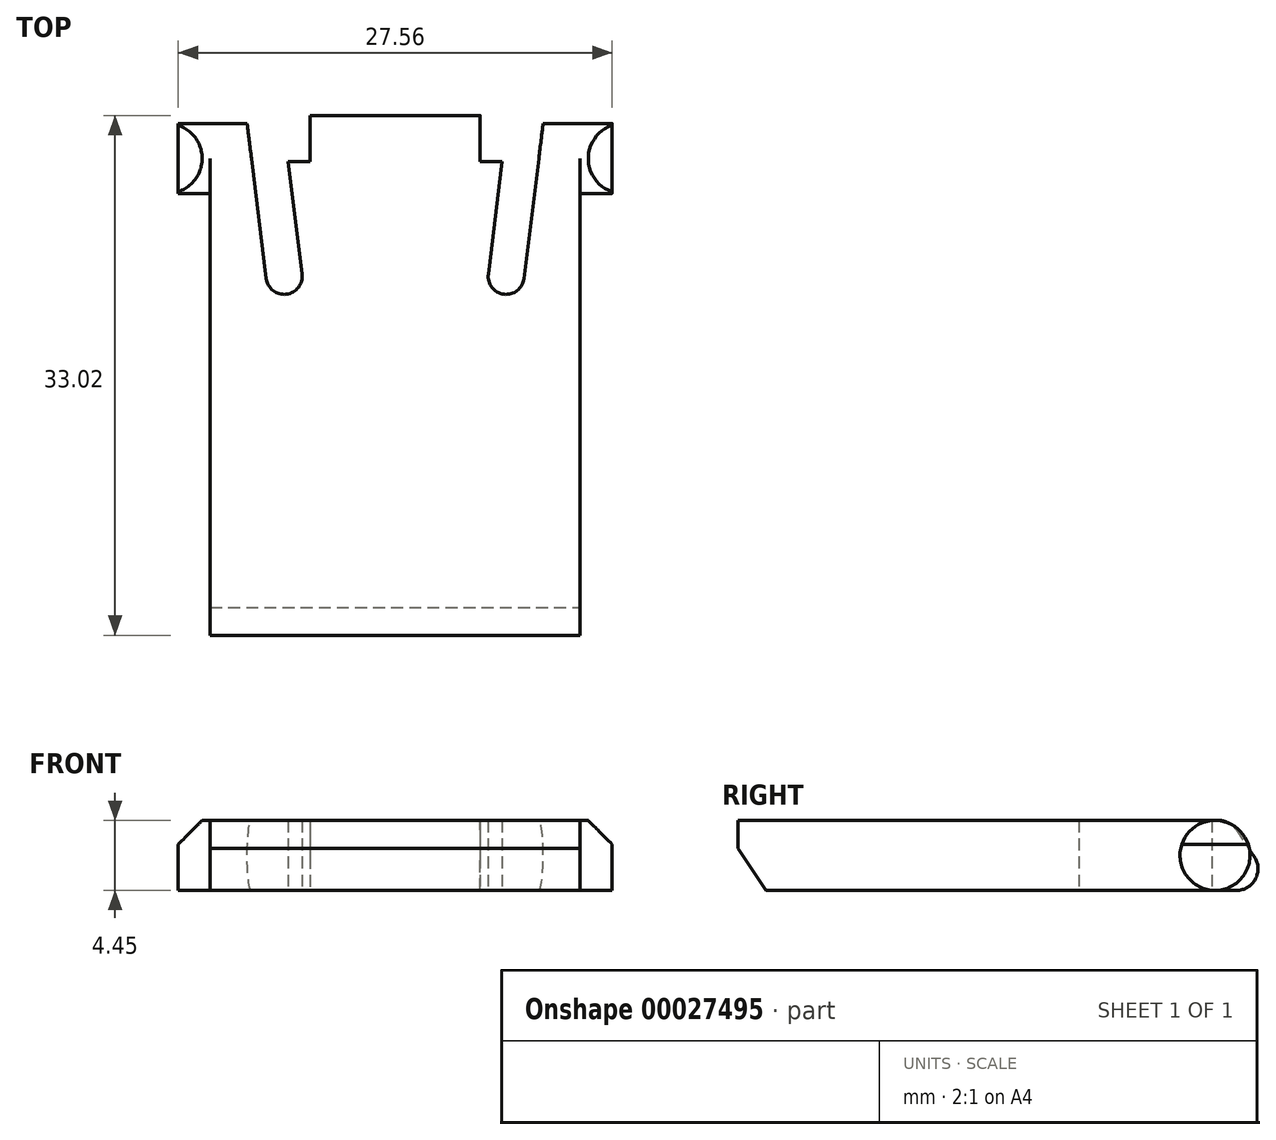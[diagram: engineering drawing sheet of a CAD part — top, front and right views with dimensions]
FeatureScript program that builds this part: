
annotation { "Feature Type Name" : "Feature", "Feature Type Description" : "" }
export const myFeature = defineFeature(function(context is Context, id is Id, definition is map)
    precondition{}
    {
        {
            var Q0;
            Q0=qCreatedBy(makeId("Top.planeOp"),FACE);
            var sketch = newSketch(context, id + "F0", { "sketchPlane" : qUnion([Q0])});
            skLineSegment(sketch, "E0.bottom", {"start": v(0, 33.02) * mm, "end": v(2.29, 33.02) * mm, "construction": true});
            skLineSegment(sketch, "E0.top", {"start": v(0, 0) * mm, "end": v(23.5, 0) * mm});
            skLineSegment(sketch, "E0.left", {"start": v(0, 33.02) * mm, "end": v(0, 32.51) * mm, "construction": true});
            skLineSegment(sketch, "E0.right", {"start": v(23.5, 33.02) * mm, "end": v(23.5, 0) * mm});
            skArc(sketch, "E1", {"start": v(3.56, 22.86) * mm, "mid": v(4.74, 21.66) * mm, "end": v(5.83, 22.94) * mm});
            skLineSegment(sketch, "E2", {"start": v(0, 22.86) * mm, "end": v(3.56, 22.86) * mm, "construction": true});
            skLineSegment(sketch, "E3", {"start": v(0.5, 33.02) * mm, "end": v(0.5, 22.86) * mm, "construction": true});
            skLineSegment(sketch, "E4", {"start": v(5.83, 22.94) * mm, "end": v(4.95, 30.1) * mm});
            skLineSegment(sketch, "E5", {"start": v(2.29, 33.02) * mm, "end": v(2.35, 32.51) * mm, "construction": true});
            skLineSegment(sketch, "E6.trimOffspring", {"start": v(6.35, 33.02) * mm, "end": v(17.15, 33.02) * mm});
            skLineSegment(sketch, "E7", {"start": v(11.75, 0) * mm, "end": v(11.75, 33.02) * mm, "construction": true});
            skLineSegment(sketch, "E8", {"start": v(4.95, 30.1) * mm, "end": v(6.35, 30.1) * mm});
            skLineSegment(sketch, "E9", {"start": v(6.35, 30.1) * mm, "end": v(6.35, 33.02) * mm});
            skLineSegment(sketch, "E10", {"start": v(0, 32.51) * mm, "end": v(2.35, 32.51) * mm});
            skLineSegment(sketch, "E11", {"start": v(2.35, 32.51) * mm, "end": v(3.56, 22.66) * mm});
            skLineSegment(sketch, "E12", {"start": v(0, 32.51) * mm, "end": v(0, 0) * mm});
            skLineSegment(sketch, "E13.MirrorCS", {"start": v(21.2, 33.02) * mm, "end": v(21.15, 32.51) * mm, "construction": true});
            skLineSegment(sketch, "E14.MirrorCS", {"start": v(23.5, 33.02) * mm, "end": v(21.2, 33.02) * mm, "construction": true});
            skLineSegment(sketch, "E15.MirrorCS", {"start": v(23.5, 33.02) * mm, "end": v(23.5, 32.51) * mm, "construction": true});
            skLineSegment(sketch, "E16.MirrorCS", {"start": v(23.5, 32.51) * mm, "end": v(21.15, 32.51) * mm});
            skLineSegment(sketch, "E17.MirrorCS", {"start": v(18.55, 30.1) * mm, "end": v(17.15, 30.1) * mm});
            skArc(sketch, "E18.MirrorCS", {"start": v(19.94, 22.86) * mm, "mid": v(18.76, 21.66) * mm, "end": v(17.66, 22.94) * mm});
            skLineSegment(sketch, "E19.MirrorCS", {"start": v(17.15, 30.1) * mm, "end": v(17.15, 33.02) * mm});
            skLineSegment(sketch, "E20.MirrorCS", {"start": v(21.15, 32.51) * mm, "end": v(19.93, 22.66) * mm});
            skLineSegment(sketch, "E21.MirrorCS", {"start": v(23, 33.02) * mm, "end": v(23, 22.86) * mm, "construction": true});
            skLineSegment(sketch, "E22.MirrorCS", {"start": v(23.5, 22.86) * mm, "end": v(19.94, 22.86) * mm, "construction": true});
            skLineSegment(sketch, "E23.MirrorCS", {"start": v(17.66, 22.94) * mm, "end": v(18.55, 30.1) * mm});
            skLineSegment(sketch, "E24.trimOffspring", {"start": v(21.2, 33.02) * mm, "end": v(23.5, 33.02) * mm, "construction": true});
            skSolve(sketch);
        }
        {
            var Q0;
            {var subQ8=sQuery(id+"F0.wireOp",EDGE,"E0.top");Q0=makeQuery(id+"F0.imprint","IMPRINT",FACE,{"disambiguationData":[TD([[makeQuery(id+"F0.imprint","IMPRINT",EDGE,{"derivedFrom":subQ8}),1.0]])]});}
            extrude(context, id + "F1", {"entities" : qUnion([Q0]), "depth" : 4.44 * mm});
        }
        {
            var Q0;
            Q0=makeQuery(id+"F1.opExtrude","SWEPT_FACE",FACE,{"disambiguationData":[OSD([sQuery(id+"F0.wireOp",EDGE,"E0.right")])]});
            var sketch = newSketch(context, id + "F2", { "sketchPlane" : qUnion([Q0])});
            skLineSegment(sketch, "E25", {"start": v(0, 2.67) * mm, "end": v(1.78, 0) * mm});
            skSolve(sketch);
        }
        {
            var Q0;
            {var subQ2=sQuery(id+"F2.wireOp",EDGE,"E25");Q0=makeQuery(id+"F2.imprint","IMPRINT",FACE,{"disambiguationData":[TD([[makeQuery(id+"F2.imprint","IMPRINT",EDGE,{"derivedFrom":subQ2}),-1.0]])]});}
            extrude(context, id + "F3", {"entities" : qUnion([Q0]), "operationType" : NewBodyOperationType.REMOVE, "endBound" : BoundingType.UP_TO_NEXT, "oppositeDirection" : true, "depth" : 25.4 * mm});
        }
        {
            var Q0;
            Q0=makeQuery(id+"F1.opExtrude","SWEPT_FACE",FACE,{"disambiguationData":[OSD([sQuery(id+"F0.wireOp",EDGE,"E19.MirrorCS")])]});
            var sketch = newSketch(context, id + "F4", { "sketchPlane" : qUnion([Q0])});
            skLineSegment(sketch, "E26", {"start": v(31.24, 4.45) * mm, "end": v(31.65, 3.84) * mm, "construction": true});
            skCircle(sketch, "E27", {"center": v(31.66, 1.36) * mm, "radius": 1.36 * mm});
            skLineSegment(sketch, "E28", {"start": v(32.8, 2.12) * mm, "end": v(33.02, 1.78) * mm, "construction": true});
            skCircle(sketch, "E29", {"center": v(30.51, 3.08) * mm, "radius": 1.36 * mm});
            skLineSegment(sketch, "E30", {"start": v(31.65, 3.84) * mm, "end": v(32.8, 2.12) * mm});
            skSolve(sketch);
        }
        {
            var Q0;
            {var subQ8=sQuery(id+"F4.wireOp",EDGE,"E30");Q0=makeQuery(id+"F4.imprint","IMPRINT",FACE,{"disambiguationData":[TD([[makeQuery(id+"F4.imprint","IMPRINT",EDGE,{"derivedFrom":subQ8}),1.0]])]});}
            var Q1;
            {var subQ0=sQuery(id+"F0.wireOp",EDGE,"E19.MirrorCS");var subQ1=makeQuery(id+"F1.opExtrude","CAP_EDGE",EDGE,{"disambiguationData":[OSD([subQ0])],"isStart":true});var subQ2=sQuery(id+"F4.wireOp",EDGE,"E27");var subQ3=makeQuery(id+"F4.imprint","INTERSECT",VERTEX,{"derivedFrom":[subQ1,subQ2]});Q1=makeQuery(id+"F4.imprint","IMPRINT",FACE,{"disambiguationData":[TD([[makeQuery(id+"F4.imprint","IMPRINT",EDGE,{"disambiguationData":[TD([[subQ3,-1.0]])],"derivedFrom":subQ2}),-1.0]])]});}
            extrude(context, id + "F5", {"entities" : qUnion([Q0, Q1]), "operationType" : NewBodyOperationType.REMOVE, "endBound" : BoundingType.UP_TO_NEXT, "oppositeDirection" : true, "depth" : 25.4 * mm});
        }
        {
            var Q0;
            Q0=makeQuery(id+"F1.opExtrude","SWEPT_FACE",FACE,{"disambiguationData":[OSD([sQuery(id+"F0.wireOp",EDGE,"E0.right")])]});
            var sketch = newSketch(context, id + "F6", { "sketchPlane" : qUnion([Q0])});
            skCircle(sketch, "E31", {"center": v(30.29, 2.22) * mm, "radius": 2.22 * mm});
            skSolve(sketch);
        }
        {
            var Q0;
            {var subQ0=sQuery(id+"F0.wireOp",EDGE,"E0.right");var subQ1=makeQuery(id+"F1.opExtrude","CAP_EDGE",EDGE,{"disambiguationData":[OSD([subQ0])],"isStart":false});var subQ2=sQuery(id+"F6.wireOp",EDGE,"E31");var subQ3=makeQuery(id+"F6.imprint","INTERSECT",VERTEX,{"derivedFrom":[subQ1,subQ2]});Q0=makeQuery(id+"F6.imprint","IMPRINT",FACE,{"disambiguationData":[TD([[makeQuery(id+"F6.imprint","IMPRINT",EDGE,{"disambiguationData":[TD([[subQ3,1.0]])],"derivedFrom":subQ2}),-1.0]])]});}
            var Q1;
            {var subQ0=sQuery(id+"F0.wireOp",EDGE,"E0.right");var subQ1=makeQuery(id+"F1.opExtrude","CAP_EDGE",EDGE,{"disambiguationData":[OSD([subQ0])],"isStart":true});var subQ2=sQuery(id+"F6.wireOp",EDGE,"E31");var subQ3=makeQuery(id+"F6.imprint","INTERSECT",VERTEX,{"derivedFrom":[subQ1,subQ2]});Q1=makeQuery(id+"F6.imprint","IMPRINT",FACE,{"disambiguationData":[TD([[makeQuery(id+"F6.imprint","IMPRINT",EDGE,{"disambiguationData":[TD([[subQ3,-1.0]])],"derivedFrom":subQ2}),-1.0]])]});}
            extrude(context, id + "F7", {"entities" : qUnion([Q0, Q1]), "operationType" : NewBodyOperationType.REMOVE, "endBound" : BoundingType.UP_TO_NEXT, "oppositeDirection" : true, "depth" : 25.4 * mm});
        }
        {
            var Q0;
            Q0=makeQuery(id+"F1.opExtrude","SWEPT_FACE",FACE,{"disambiguationData":[OSD([sQuery(id+"F0.wireOp",EDGE,"E12")])]});
            var sketch = newSketch(context, id + "F8", { "sketchPlane" : qUnion([Q0])});
            skCircle(sketch, "E32", {"center": v(-30.29, 2.22) * mm, "radius": 2.22 * mm});
            skSolve(sketch);
        }
        {
            var Q0;
            {var subQ0=sQuery(id+"F0.wireOp",EDGE,"E12");var subQ1=makeQuery(id+"F1.opExtrude","CAP_EDGE",EDGE,{"disambiguationData":[OSD([subQ0])],"isStart":false});var subQ2=sQuery(id+"F8.wireOp",EDGE,"E32");var subQ3=makeQuery(id+"F8.imprint","INTERSECT",VERTEX,{"derivedFrom":[subQ1,subQ2]});Q0=makeQuery(id+"F8.imprint","IMPRINT",FACE,{"disambiguationData":[TD([[makeQuery(id+"F8.imprint","IMPRINT",EDGE,{"disambiguationData":[TD([[subQ3,-1.0]])],"derivedFrom":subQ2}),-1.0]])]});}
            var Q1;
            {var subQ0=sQuery(id+"F0.wireOp",EDGE,"E12");var subQ1=makeQuery(id+"F1.opExtrude","CAP_EDGE",EDGE,{"disambiguationData":[OSD([subQ0])],"isStart":true});var subQ2=sQuery(id+"F8.wireOp",EDGE,"E32");var subQ3=makeQuery(id+"F8.imprint","INTERSECT",VERTEX,{"derivedFrom":[subQ1,subQ2]});Q1=makeQuery(id+"F8.imprint","IMPRINT",FACE,{"disambiguationData":[TD([[makeQuery(id+"F8.imprint","IMPRINT",EDGE,{"disambiguationData":[TD([[subQ3,1.0]])],"derivedFrom":subQ2}),-1.0]])]});}
            extrude(context, id + "F9", {"entities" : qUnion([Q0, Q1]), "operationType" : NewBodyOperationType.REMOVE, "endBound" : BoundingType.UP_TO_NEXT, "oppositeDirection" : true, "depth" : 25.4 * mm});
        }
        {
            var Q0;
            Q0=makeQuery(id+"F1.opExtrude","SWEPT_FACE",FACE,{"disambiguationData":[OSD([sQuery(id+"F0.wireOp",EDGE,"E12")])]});
            var sketch = newSketch(context, id + "F10", { "sketchPlane" : qUnion([Q0])});
            skCircle(sketch, "E33", {"center": v(-30.29, 2.22) * mm, "radius": 2.22 * mm});
            skSolve(sketch);
        }
        {
            var Q0;
            {var subQ0=sQuery(id+"F10.wireOp",EDGE,"E33");var subQ1=sQuery(id+"F0.wireOp",EDGE,"E12");var subQ3=makeQuery(id+"F10.imprint","INTERSECT",VERTEX,{"derivedFrom":[makeQuery(id+"F1.opExtrude","CAP_EDGE",EDGE,{"disambiguationData":[OSD([subQ1])],"isStart":false}),subQ0]});Q0=makeQuery(id+"F10.imprint","IMPRINT",FACE,{"disambiguationData":[TD([[makeQuery(id+"F10.imprint","IMPRINT",EDGE,{"disambiguationData":[TD([[subQ3,-1.0]])],"derivedFrom":subQ0}),1.0]])]});}
            extrude(context, id + "F11", {"entities" : qUnion([Q0]), "operationType" : NewBodyOperationType.ADD, "depth" : 2.03 * mm});
        }
        {
            var Q0;
            Q0=makeQuery(id+"F1.opExtrude","SWEPT_FACE",FACE,{"disambiguationData":[OSD([sQuery(id+"F0.wireOp",EDGE,"E0.right")])]});
            var sketch = newSketch(context, id + "F12", { "sketchPlane" : qUnion([Q0])});
            skCircle(sketch, "E34", {"center": v(30.29, 2.22) * mm, "radius": 2.22 * mm});
            skSolve(sketch);
        }
        {
            var Q0;
            {var subQ0=sQuery(id+"F12.wireOp",EDGE,"E34");var subQ1=sQuery(id+"F0.wireOp",EDGE,"E0.right");var subQ3=makeQuery(id+"F12.imprint","INTERSECT",VERTEX,{"derivedFrom":[makeQuery(id+"F1.opExtrude","CAP_EDGE",EDGE,{"disambiguationData":[OSD([subQ1])],"isStart":false}),subQ0]});Q0=makeQuery(id+"F12.imprint","IMPRINT",FACE,{"disambiguationData":[TD([[makeQuery(id+"F12.imprint","IMPRINT",EDGE,{"disambiguationData":[TD([[subQ3,-1.0]])],"derivedFrom":subQ0}),1.0]])]});}
            extrude(context, id + "F13", {"entities" : qUnion([Q0]), "operationType" : NewBodyOperationType.ADD, "depth" : 2.03 * mm});
        }
        {
            var Q0;
            Q0=makeQuery(id+"F1.opExtrude","SWEPT_FACE",FACE,{"disambiguationData":[OSD([sQuery(id+"F0.wireOp",EDGE,"E0.top")])]});
            var sketch = newSketch(context, id + "F14", { "sketchPlane" : qUnion([Q0])});
            skLineSegment(sketch, "E35.bottom", {"start": v(0, 4.45) * mm, "end": v(-2.03, 4.45) * mm});
            skLineSegment(sketch, "E35.top", {"start": v(0, 0) * mm, "end": v(-2.03, 0) * mm, "construction": true});
            skLineSegment(sketch, "E35.left", {"start": v(0, 4.45) * mm, "end": v(0, 0) * mm});
            skLineSegment(sketch, "E35.right", {"start": v(-2.03, 4.45) * mm, "end": v(-2.03, 0) * mm});
            skLineSegment(sketch, "E36", {"start": v(11.75, 4.45) * mm, "end": v(11.75, 2.67) * mm, "construction": true});
            skLineSegment(sketch, "E37", {"start": v(-0.5, 4.45) * mm, "end": v(-2.03, 2.92) * mm});
            skLineSegment(sketch, "E38.MirrorCS", {"start": v(23.5, 4.45) * mm, "end": v(23.5, 0) * mm});
            skLineSegment(sketch, "E39.MirrorCS", {"start": v(23.5, 0) * mm, "end": v(25.53, 0) * mm, "construction": true});
            skLineSegment(sketch, "E40.MirrorCS", {"start": v(23.5, 4.45) * mm, "end": v(25.53, 4.45) * mm});
            skLineSegment(sketch, "E41.MirrorCS", {"start": v(24, 4.45) * mm, "end": v(25.53, 2.92) * mm});
            skLineSegment(sketch, "E42.MirrorCS", {"start": v(25.53, 4.45) * mm, "end": v(25.53, 0) * mm});
            skSolve(sketch);
        }
        {
            var Q0;
            {var subQ0=sQuery(id+"F14.wireOp",EDGE,"E37");Q0=makeQuery(id+"F14.imprint","IMPRINT",FACE,{"disambiguationData":[TD([[makeQuery(id+"F14.imprint","IMPRINT",EDGE,{"derivedFrom":subQ0}),-1.0]])]});}
            var Q1;
            {var subQ1=sQuery(id+"F14.wireOp",EDGE,"E41.MirrorCS");Q1=makeQuery(id+"F14.imprint","IMPRINT",FACE,{"disambiguationData":[TD([[makeQuery(id+"F14.imprint","IMPRINT",EDGE,{"derivedFrom":subQ1}),1.0]])]});}
            extrude(context, id + "F15", {"entities" : qUnion([Q0, Q1]), "operationType" : NewBodyOperationType.REMOVE, "endBound" : BoundingType.THROUGH_ALL, "oppositeDirection" : true, "depth" : 25.4 * mm});
        }
    });
